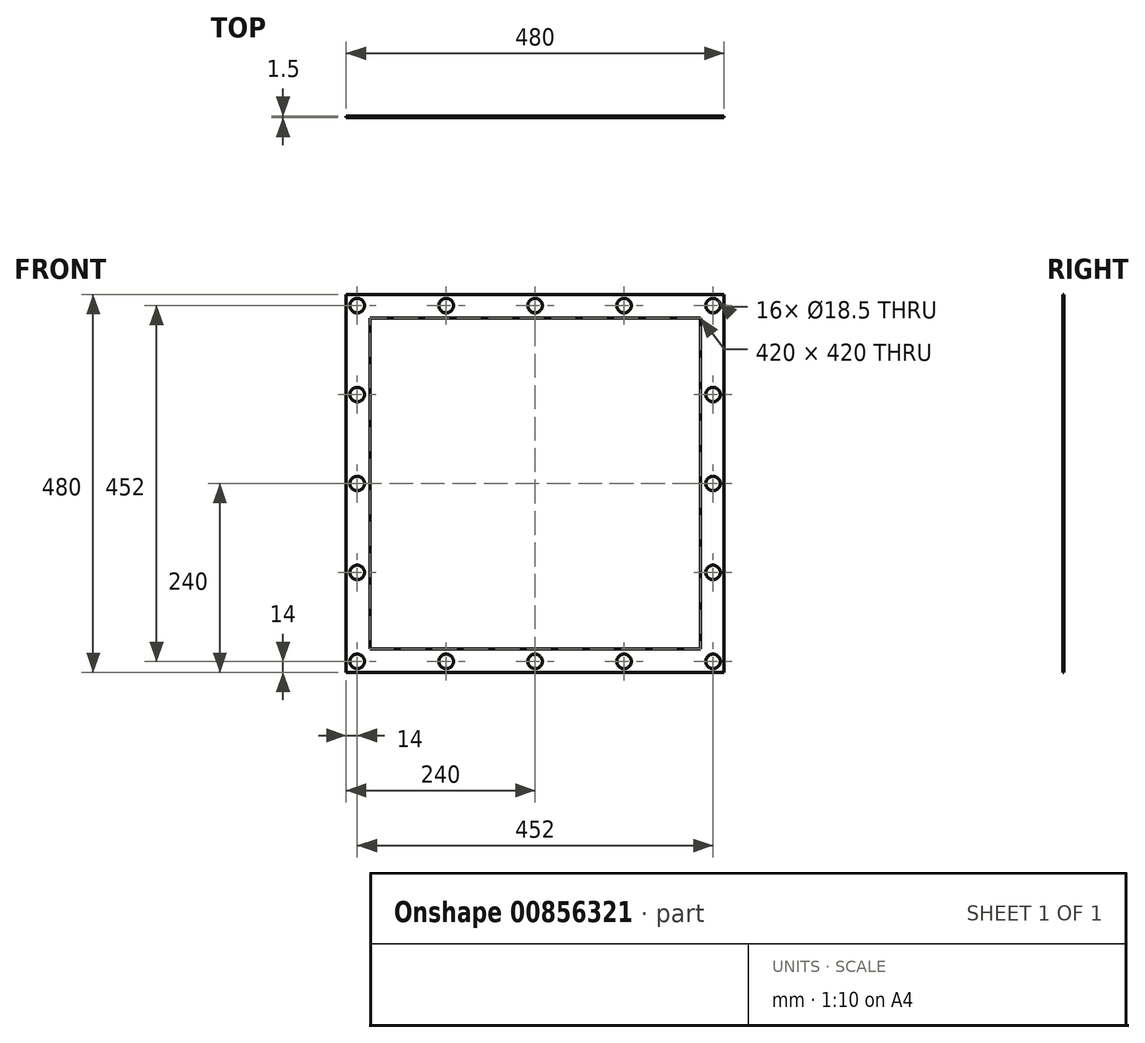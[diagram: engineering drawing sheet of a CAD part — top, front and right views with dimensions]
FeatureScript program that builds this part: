
annotation { "Feature Type Name" : "Feature", "Feature Type Description" : "" }
export const myFeature = defineFeature(function(context is Context, id is Id, definition is map)
    precondition{}
    {
        {
            var Q0;
            Q0=qCreatedBy(makeId("Front.planeOp"),FACE);
            var sketch = newSketch(context, id + "F0", { "sketchPlane" : qUnion([Q0])});
            skLineSegment(sketch, "E0", {"start": v(0, 343.8) * mm, "end": v(0, -363.23) * mm, "construction": true});
            skLineSegment(sketch, "E1", {"start": v(-395.89, 0) * mm, "end": v(423.56, 0) * mm, "construction": true});
            skLineSegment(sketch, "E2.bottom", {"start": v(-210, 210) * mm, "end": v(210, 210) * mm});
            skLineSegment(sketch, "E2.top", {"start": v(-210, -210) * mm, "end": v(210, -210) * mm});
            skLineSegment(sketch, "E2.left", {"start": v(-210, 210) * mm, "end": v(-210, -210) * mm});
            skLineSegment(sketch, "E2.right", {"start": v(210, 210) * mm, "end": v(210, -210) * mm});
            skLineSegment(sketch, "E3.0", {"start": v(-240, 240) * mm, "end": v(240, 240) * mm});
            skLineSegment(sketch, "E3.1", {"start": v(-240, 240) * mm, "end": v(-240, -240) * mm});
            skLineSegment(sketch, "E3.2", {"start": v(-240, -240) * mm, "end": v(240, -240) * mm});
            skLineSegment(sketch, "E3.3", {"start": v(240, 240) * mm, "end": v(240, -240) * mm});
            skSolve(sketch);
        }
        {
            var Q0;
            Q0 = qSketchRegion(id + "F0", true);
            extrude(context, id + "F1", {"entities" : qUnion([Q0]), "depth" : 1.5 * mm, "offsetDistance" : 25 * mm});
        }
        {
            var Q0;
            Q0=makeQuery(id+"F1.opExtrude","CAP_FACE",FACE,{"disambiguationData":[OSD([sQuery(id+"F0.wireOp",EDGE,"E2.bottom"),sQuery(id+"F0.wireOp",EDGE,"E2.top"),sQuery(id+"F0.wireOp",EDGE,"E2.left"),sQuery(id+"F0.wireOp",EDGE,"E2.right"),sQuery(id+"F0.wireOp",EDGE,"E3.0"),sQuery(id+"F0.wireOp",EDGE,"E3.1"),sQuery(id+"F0.wireOp",EDGE,"E3.2"),sQuery(id+"F0.wireOp",EDGE,"E3.3")])],"isStart":false});
            var sketch = newSketch(context, id + "F2", { "sketchPlane" : qUnion([Q0])});
            skLineSegment(sketch, "E4.0", {"start": v(-226, 226) * mm, "end": v(226, 226) * mm, "construction": true});
            skLineSegment(sketch, "E4.1", {"start": v(-226, 226) * mm, "end": v(-226, -226) * mm, "construction": true});
            skLineSegment(sketch, "E4.2", {"start": v(-226, -226) * mm, "end": v(226, -226) * mm, "construction": true});
            skLineSegment(sketch, "E4.3", {"start": v(226, 226) * mm, "end": v(226, -226) * mm, "construction": true});
            skLineSegment(sketch, "E5", {"start": v(0, 129.01) * mm, "end": v(0, -150.46) * mm, "construction": true});
            skLineSegment(sketch, "E6", {"start": v(-164.71, 0) * mm, "end": v(163.44, 0) * mm, "construction": true});
            skCircle(sketch, "E7", {"center": v(-226, 226) * mm, "radius": 9.25 * mm});
            skCircle(sketch, "E8.1.0.0", {"center": v(-113, 226) * mm, "radius": 9.25 * mm});
            skCircle(sketch, "E8.2.0.0", {"center": v(0, 226) * mm, "radius": 9.25 * mm});
            skCircle(sketch, "E8.3.0.0", {"center": v(113, 226) * mm, "radius": 9.25 * mm});
            skCircle(sketch, "E8.4.0.0", {"center": v(226, 226) * mm, "radius": 9.25 * mm});
            skLineSegment(sketch, "E8.direction1", {"start": v(-226, 226) * mm, "end": v(-113, 226) * mm, "construction": true});
            skCircle(sketch, "E9.0.1.0", {"center": v(-226, 113) * mm, "radius": 9.25 * mm});
            skCircle(sketch, "E9.0.2.0", {"center": v(-226, 0) * mm, "radius": 9.25 * mm});
            skCircle(sketch, "E9.0.3.0", {"center": v(-226, -113) * mm, "radius": 9.25 * mm});
            skCircle(sketch, "E9.0.4.0", {"center": v(-226, -226) * mm, "radius": 9.25 * mm});
            skLineSegment(sketch, "E9.direction1", {"start": v(-226, 226) * mm, "end": v(-201, 226) * mm, "construction": true});
            skLineSegment(sketch, "E9.direction2", {"start": v(-226, 226) * mm, "end": v(-226, 113) * mm, "construction": true});
            skCircle(sketch, "E10.MirrorC", {"center": v(-113, -226) * mm, "radius": 9.25 * mm});
            skCircle(sketch, "E11.MirrorC", {"center": v(0, -226) * mm, "radius": 9.25 * mm});
            skCircle(sketch, "E12.MirrorC", {"center": v(113, -226) * mm, "radius": 9.25 * mm});
            skCircle(sketch, "E13.MirrorC", {"center": v(226, -226) * mm, "radius": 9.25 * mm});
            skCircle(sketch, "E14.MirrorC", {"center": v(226, 113) * mm, "radius": 9.25 * mm});
            skCircle(sketch, "E15.MirrorC", {"center": v(226, 0) * mm, "radius": 9.25 * mm});
            skCircle(sketch, "E16.MirrorC", {"center": v(226, -113) * mm, "radius": 9.25 * mm});
            skSolve(sketch);
        }
        {
            var Q0;
            Q0 = qSketchRegion(id + "F2", true);
            extrude(context, id + "F3", {"entities" : qUnion([Q0]), "operationType" : NewBodyOperationType.REMOVE, "endBound" : BoundingType.UP_TO_NEXT, "oppositeDirection" : true, "depth" : 25 * mm, "offsetDistance" : 25 * mm});
        }
    });
